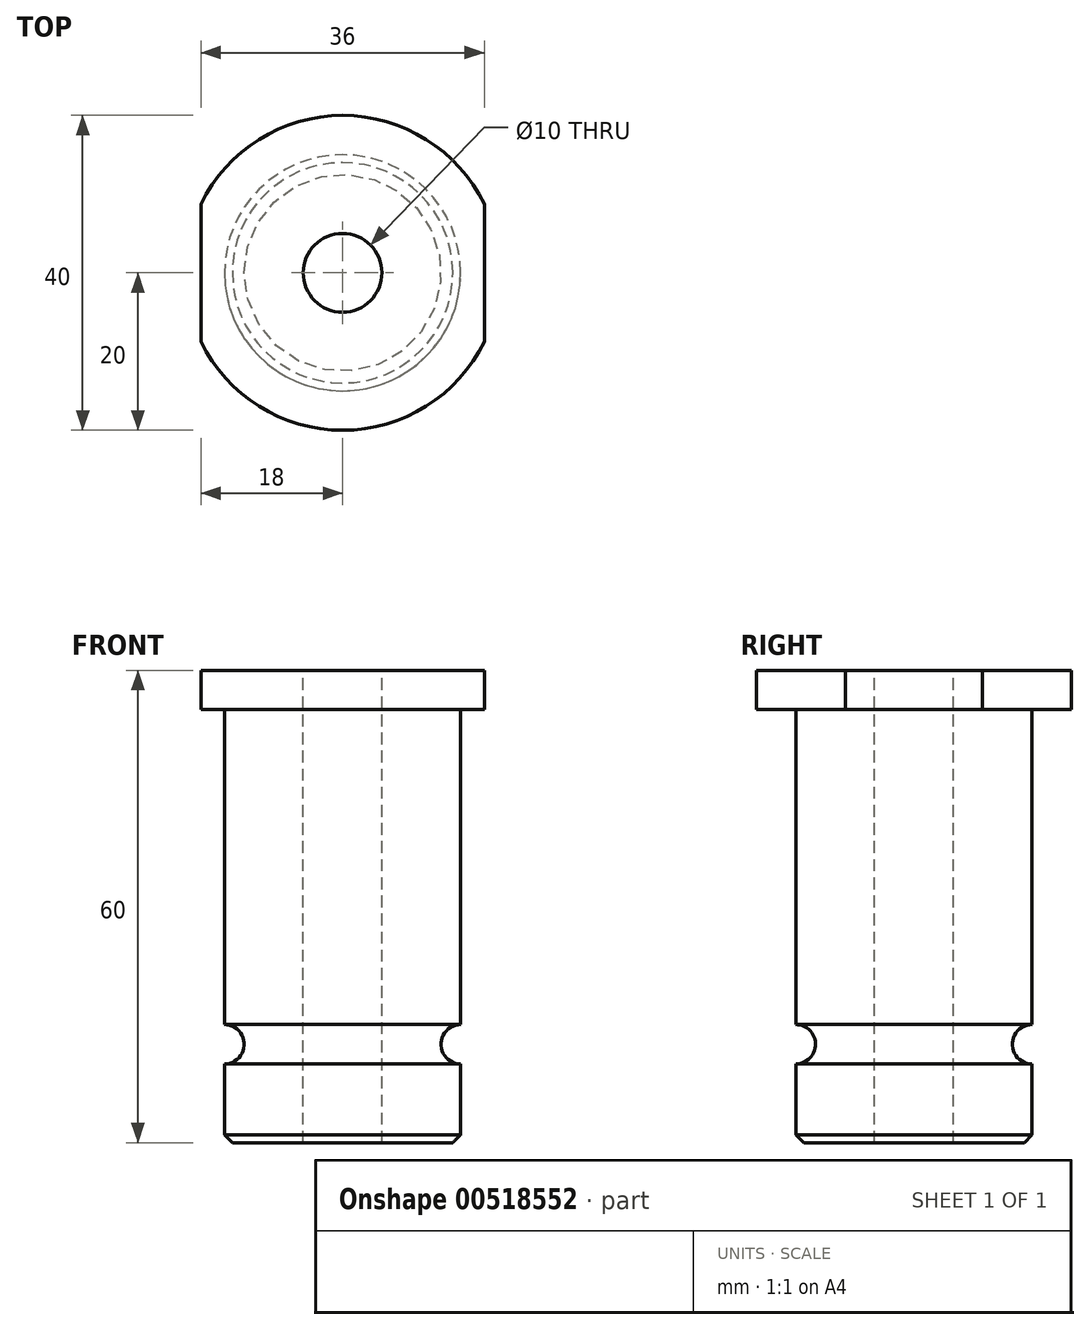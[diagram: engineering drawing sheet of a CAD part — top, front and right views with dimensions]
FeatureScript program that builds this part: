
annotation { "Feature Type Name" : "Feature", "Feature Type Description" : "" }
export const myFeature = defineFeature(function(context is Context, id is Id, definition is map)
    precondition{}
    {
        {
            assignVariable(context, id + "F0", {"name" : "a", "anyValue" : 55});
        }
        {
            var Q0;
            Q0=qCreatedBy(makeId("Top.planeOp"),FACE);
            var sketch = newSketch(context, id + "F1", { "sketchPlane" : qUnion([Q0])});
            skCircle(sketch, "E0", {"center": v(0, 0) * mm, "radius": 15 * mm});
            skSolve(sketch);
        }
        {
            var Q0;
            Q0=qSketchRegion(id+"F1",true);
            extrude(context, id + "F2", {"entities" : qUnion([Q0]), "depth" : (getVariable(context, 'a')) * mm, "offsetDistance" : 25 * mm});
        }
        {
            var Q0;
            Q0=makeQuery(id+"F2.opExtrude","CAP_FACE",FACE,{"disambiguationData":[OSD([sQuery(id+"F1.wireOp",EDGE,"E0")])],"isStart":false});
            var sketch = newSketch(context, id + "F3", { "sketchPlane" : qUnion([Q0])});
            skCircle(sketch, "E1", {"center": v(0, 0) * mm, "radius": 20 * mm});
            skSolve(sketch);
        }
        {
            var Q0;
            Q0=makeQuery(id+"F2.opExtrude","CAP_FACE",FACE,{"disambiguationData":[OSD([sQuery(id+"F1.wireOp",EDGE,"E0")])],"isStart":true});
            cPlane(context, id + "F4", {"entities" : qUnion([Q0]), "cplaneType" : CPlaneType.OFFSET, "offset" : 60 * mm, "oppositeDirection" : true, "width" : 150 * mm, "height" : 150 * mm});
        }
        {
            var Q0;
            Q0=qSketchRegion(id+"F3",true);
            var Q1;
            Q1=qCreatedBy(id+"F4.planeOp",FACE);
            extrude(context, id + "F5", {"entities" : qUnion([Q0]), "operationType" : NewBodyOperationType.ADD, "endBound" : BoundingType.UP_TO_SURFACE, "depth" : 25 * mm, "endBoundEntityFace" : qUnion([Q1]), "offsetDistance" : 25 * mm});
        }
        {
            var Q0;
            Q0=makeQuery(id+"F5.opExtrude","CAP_FACE",FACE,{"disambiguationData":[OSD([sQuery(id+"F3.wireOp",EDGE,"E1")])],"isStart":false});
            var sketch = newSketch(context, id + "F6", { "sketchPlane" : qUnion([Q0])});
            skCircle(sketch, "E2", {"center": v(0, 0) * mm, "radius": 5 * mm});
            skSolve(sketch);
        }
        {
            var Q0;
            Q0=qSketchRegion(id+"F6",true);
            extrude(context, id + "F7", {"entities" : qUnion([Q0]), "operationType" : NewBodyOperationType.REMOVE, "endBound" : BoundingType.THROUGH_ALL, "oppositeDirection" : true, "depth" : 25 * mm, "offsetDistance" : 25 * mm});
        }
        {
            var Q0;
            Q0=makeQuery(id+"F5.opExtrude","CAP_FACE",FACE,{"disambiguationData":[OSD([sQuery(id+"F3.wireOp",EDGE,"E1")])],"isStart":false});
            var sketch = newSketch(context, id + "F8", { "sketchPlane" : qUnion([Q0])});
            skLineSegment(sketch, "E3", {"start": v(-18, 0) * mm, "end": v(18, 0) * mm});
            skLineSegment(sketch, "E4", {"start": v(-18, -8.72) * mm, "end": v(-18, 8.72) * mm});
            skLineSegment(sketch, "E5", {"start": v(18, 8.72) * mm, "end": v(18, -8.72) * mm});
            skSolve(sketch);
        }
        {
            var Q0;
            Q0=qSketchRegion(id+"F8",true);
            var Q1;
            {var subQ0=sQuery(id+"F8.wireOp",EDGE,"E4");var subQ1=makeQuery(id+"F8.imprint","INTERSECT",VERTEX,{"derivedFrom":[sQuery(id+"F8.wireOp",EDGE,"E3"),subQ0]});Q1=makeQuery(id+"F8.imprint","IMPRINT",FACE,{"disambiguationData":[TD([[makeQuery(id+"F8.imprint","IMPRINT",EDGE,{"disambiguationData":[TD([[subQ1,1.0]])],"derivedFrom":subQ0}),1.0]])]});}
            var Q2;
            {var subQ0=sQuery(id+"F8.wireOp",EDGE,"E5");var subQ1=makeQuery(id+"F8.imprint","INTERSECT",VERTEX,{"derivedFrom":[sQuery(id+"F8.wireOp",EDGE,"E3"),subQ0]});Q2=makeQuery(id+"F8.imprint","IMPRINT",FACE,{"disambiguationData":[TD([[makeQuery(id+"F8.imprint","IMPRINT",EDGE,{"disambiguationData":[TD([[subQ1,1.0]])],"derivedFrom":subQ0}),1.0]])]});}
            extrude(context, id + "F9", {"entities" : qUnion([Q0, Q1, Q2]), "operationType" : NewBodyOperationType.REMOVE, "endBound" : BoundingType.THROUGH_ALL, "oppositeDirection" : true, "depth" : 25 * mm, "offsetDistance" : 25 * mm});
        }
        {
            var Q0;
            Q0=qCreatedBy(makeId("Right.planeOp"),FACE);
            var sketch = newSketch(context, id + "F10", { "sketchPlane" : qUnion([Q0])});
            skCircle(sketch, "E6", {"center": v(-15, 12.5) * mm, "radius": 2.5 * mm});
            skLineSegment(sketch, "E7", {"start": v(0, 60.3) * mm, "end": v(0, -4.76) * mm, "construction": true});
            skSolve(sketch);
        }
        {
            var Q0;
            Q0=qSketchRegion(id+"F10",true);
            var Q1;
            Q1=makeQuery(id+"F2.opExtrude","SWEPT_FACE",FACE,{"disambiguationData":[OSD([sQuery(id+"F1.wireOp",EDGE,"E0")])]});
            revolve(context, id + "F11", {"operationType" : NewBodyOperationType.REMOVE, "entities" : qUnion([Q0]), "axis" : qUnion([Q1]), "revolveType" : RevolveType.FULL, "oppositeDirection" : true});
        }
        {
            var Q0;
            Q0=makeQuery(id+"F2.opExtrude","CAP_EDGE",EDGE,{"disambiguationData":[OSD([sQuery(id+"F1.wireOp",EDGE,"E0")])],"isStart":true});
            chamfer(context, id + "F12", {"entities" : qUnion([Q0]), "width" : 1 * mm, "tangentPropagation" : true});
        }
    });
